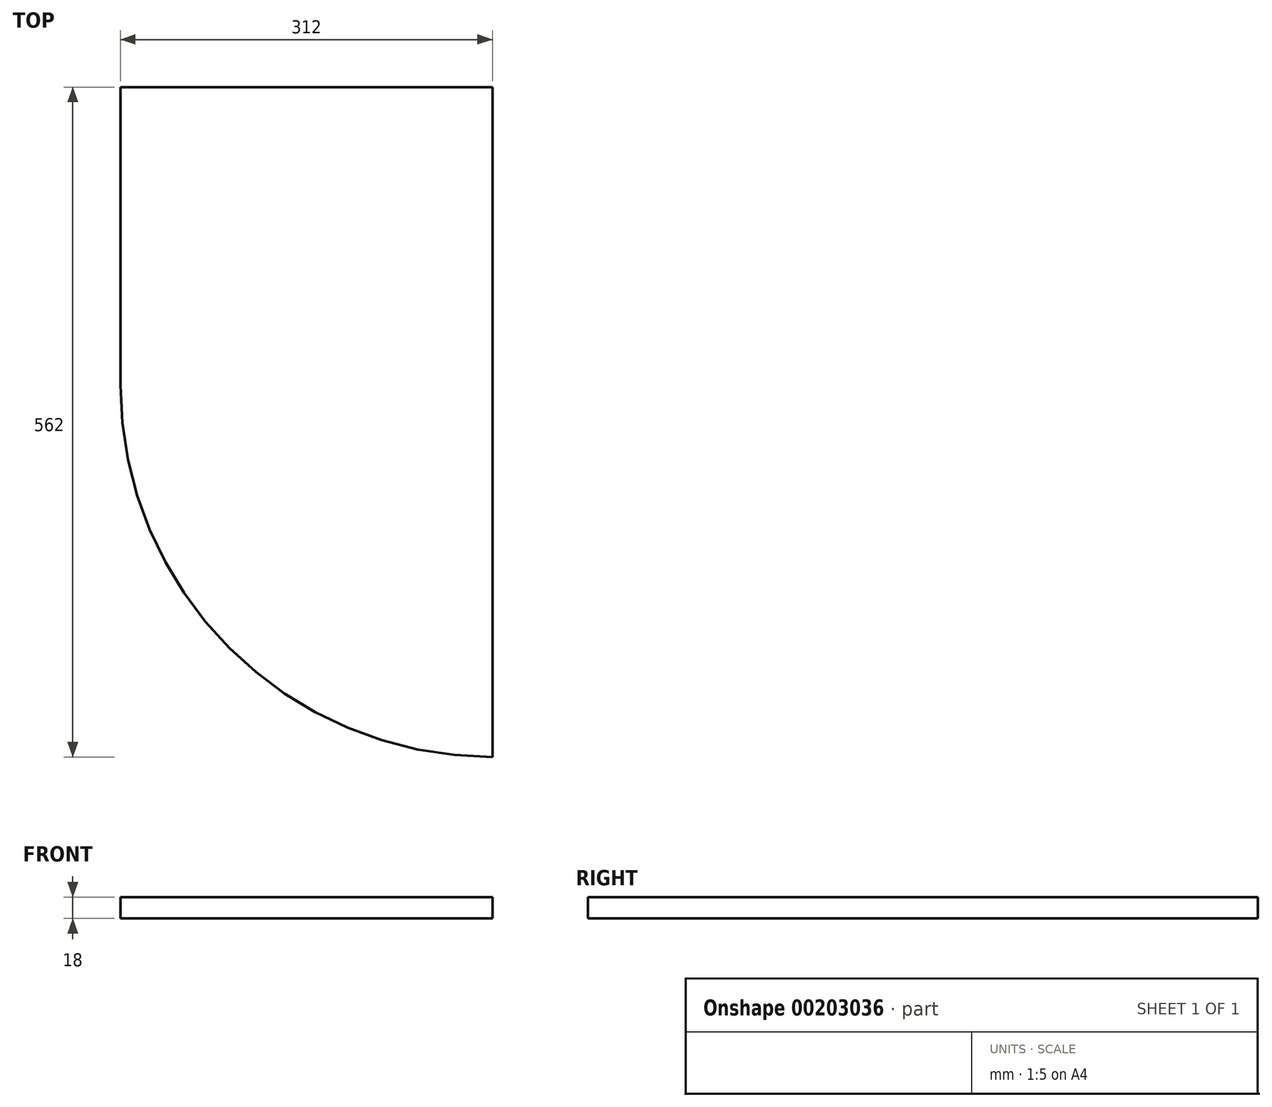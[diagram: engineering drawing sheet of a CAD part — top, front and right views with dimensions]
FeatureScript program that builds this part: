
annotation { "Feature Type Name" : "Feature", "Feature Type Description" : "" }
export const myFeature = defineFeature(function(context is Context, id is Id, definition is map)
    precondition{}
    {
        {
            var Q0;
            Q0=qCreatedBy(makeId("Top.planeOp"),FACE);
            var sketch = newSketch(context, id + "F0", { "sketchPlane" : qUnion([Q0])});
            skLineSegment(sketch, "E0", {"start": v(0, 0) * mm, "end": v(0, 562) * mm});
            skLineSegment(sketch, "E1", {"start": v(0, 562) * mm, "end": v(-312, 562) * mm});
            skLineSegment(sketch, "E2", {"start": v(-312, 562) * mm, "end": v(-312, 312) * mm});
            skArc(sketch, "E3", {"start": v(-312, 312) * mm, "mid": v(-220.62, 91.38) * mm, "end": v(0, 0) * mm});
            skSolve(sketch);
        }
        {
            var Q0;
            Q0=qSketchRegion(id+"F0",true);
            extrude(context, id + "F1", {"entities" : qUnion([Q0]), "depth" : 18 * mm});
        }
    });
